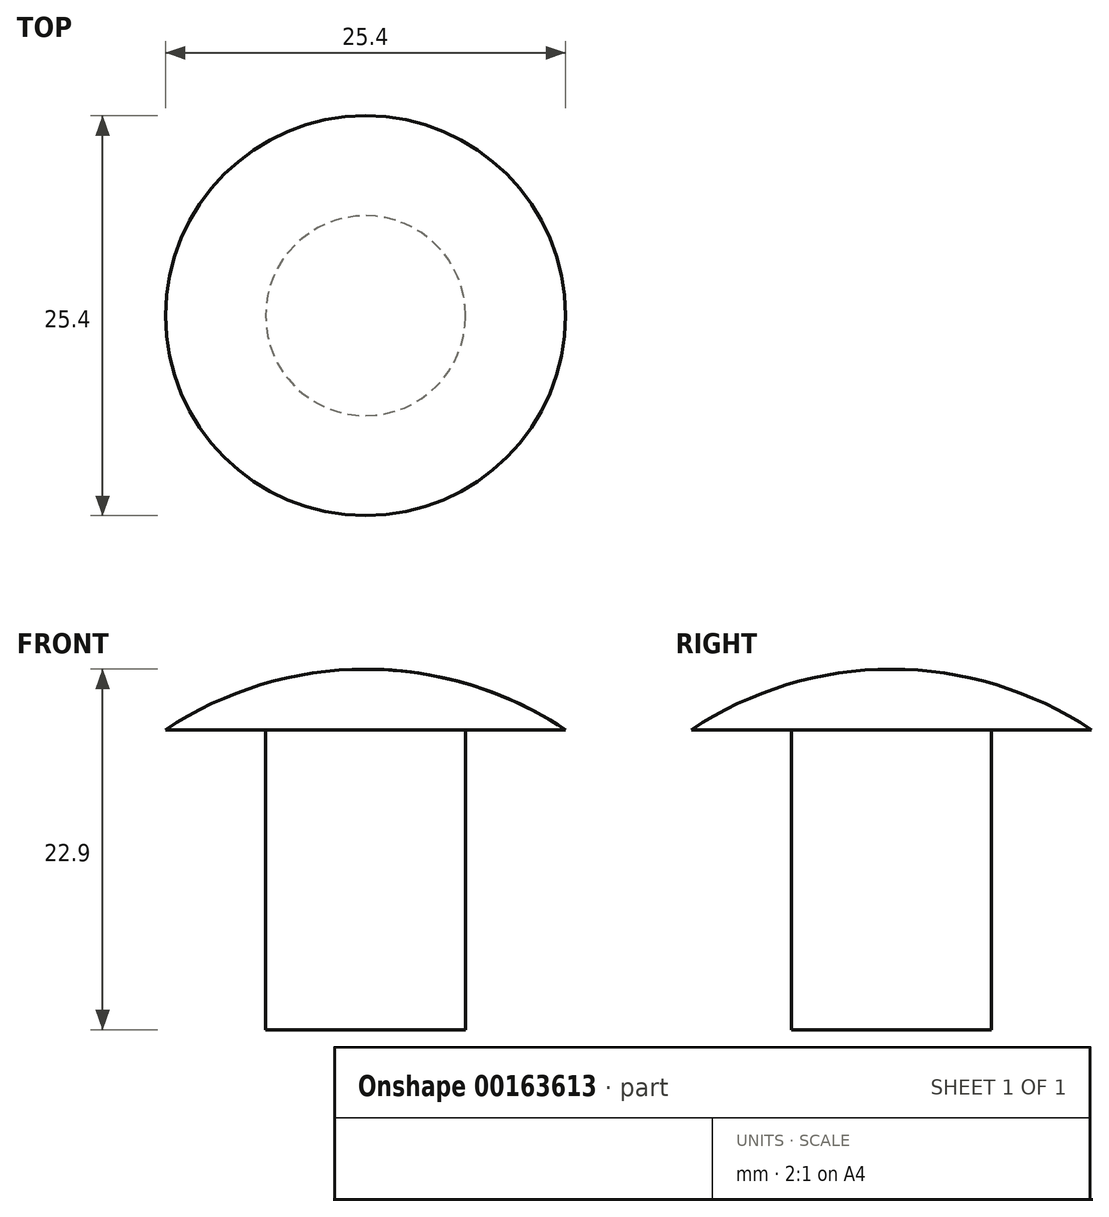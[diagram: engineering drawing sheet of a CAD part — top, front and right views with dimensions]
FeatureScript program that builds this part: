
annotation { "Feature Type Name" : "Feature", "Feature Type Description" : "" }
export const myFeature = defineFeature(function(context is Context, id is Id, definition is map)
    precondition{}
    {
        {
            var Q0;
            Q0=qCreatedBy(makeId("Front.planeOp"),FACE);
            var sketch = newSketch(context, id + "F0", { "sketchPlane" : qUnion([Q0])});
            skLineSegment(sketch, "E0", {"start": v(0, 0) * mm, "end": v(6.35, 0) * mm});
            skLineSegment(sketch, "E1", {"start": v(6.35, 0) * mm, "end": v(6.35, 19.05) * mm});
            skLineSegment(sketch, "E2", {"start": v(6.35, 19.05) * mm, "end": v(12.7, 19.05) * mm});
            skArc(sketch, "E3", {"start": v(12.7, 19.05) * mm, "mid": v(6.63, 21.91) * mm, "end": v(0, 22.9) * mm});
            skLineSegment(sketch, "E4", {"start": v(0, 22.9) * mm, "end": v(0, 0) * mm});
            skLineSegment(sketch, "E5", {"start": v(0, 53.01) * mm, "end": v(0, -69.42) * mm, "construction": true});
            skSolve(sketch);
        }
        {
            var Q0;
            Q0=makeQuery(id+"F0.imprint","IMPRINT",FACE,{"disambiguationData":[TD([[makeQuery(id+"F0.imprint","IMPRINT",EDGE,{"derivedFrom":sQuery(id+"F0.wireOp",EDGE,"E0")}),1.0]])]});
            var Q1;
            Q1=sQuery(id+"F0.wireOp",EDGE,"E5");
            revolve(context, id + "F1", {"entities" : qUnion([Q0]), "axis" : qUnion([Q1]), "revolveType" : RevolveType.FULL});
        }
    });
